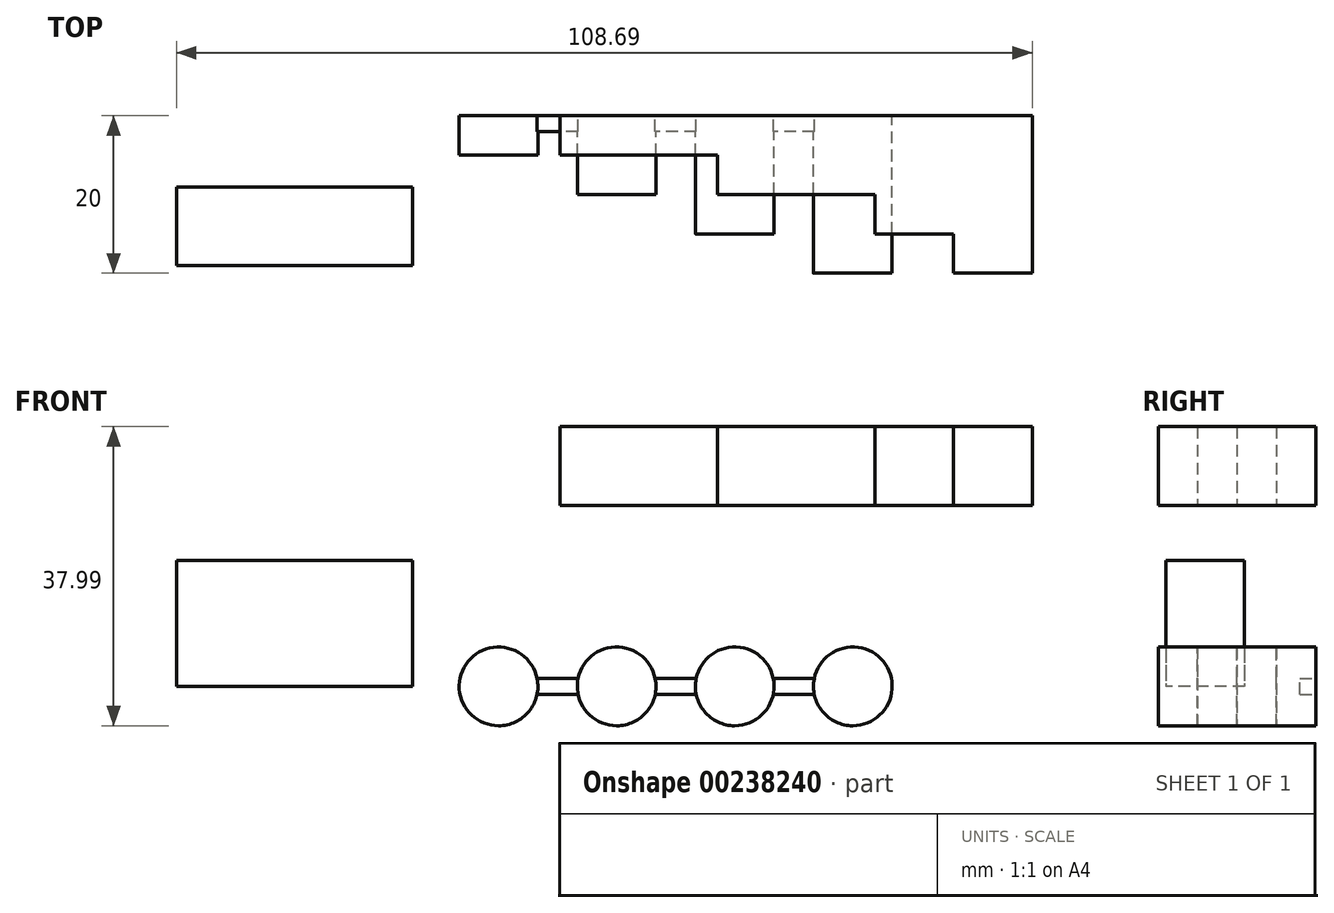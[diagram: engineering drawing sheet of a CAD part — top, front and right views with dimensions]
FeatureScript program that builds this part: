
annotation { "Feature Type Name" : "Feature", "Feature Type Description" : "" }
export const myFeature = defineFeature(function(context is Context, id is Id, definition is map)
    precondition{}
    {
        {
            var Q0;
            Q0=qCreatedBy(makeId("Front.planeOp"),FACE);
            var sketch = newSketch(context, id + "F0", { "sketchPlane" : qUnion([Q0])});
            skCircle(sketch, "E0", {"center": v(0, 0) * mm, "radius": 5 * mm});
            skCircle(sketch, "E1.1.0.0", {"center": v(15, 0) * mm, "radius": 5 * mm});
            skCircle(sketch, "E1.2.0.0", {"center": v(30, 0) * mm, "radius": 5 * mm});
            skCircle(sketch, "E1.3.0.0", {"center": v(45, 0) * mm, "radius": 5 * mm});
            skLineSegment(sketch, "E1.direction1", {"start": v(0, 0) * mm, "end": v(15, 0) * mm, "construction": true});
            skSolve(sketch);
        }
        {
            var Q0;
            Q0=makeQuery(id+"F0.imprint","IMPRINT",FACE,{"disambiguationData":[TD([[makeQuery(id+"F0.imprint","IMPRINT",EDGE,{"derivedFrom":sQuery(id+"F0.wireOp",EDGE,"E0")}),1.0]])]});
            extrude(context, id + "F1", {"entities" : qUnion([Q0]), "depth" : 5 * mm});
        }
        {
            var Q0;
            Q0=makeQuery(id+"F0.imprint","IMPRINT",FACE,{"disambiguationData":[TD([[makeQuery(id+"F0.imprint","IMPRINT",EDGE,{"derivedFrom":sQuery(id+"F0.wireOp",EDGE,"E1.1.0.0")}),1.0]])]});
            extrude(context, id + "F2", {"entities" : qUnion([Q0]), "depth" : 10 * mm});
        }
        {
            var Q0;
            Q0=makeQuery(id+"F0.imprint","IMPRINT",FACE,{"disambiguationData":[TD([[makeQuery(id+"F0.imprint","IMPRINT",EDGE,{"derivedFrom":sQuery(id+"F0.wireOp",EDGE,"E1.2.0.0")}),1.0]])]});
            extrude(context, id + "F3", {"entities" : qUnion([Q0]), "depth" : 15 * mm});
        }
        {
            var Q0;
            Q0=makeQuery(id+"F0.imprint","IMPRINT",FACE,{"disambiguationData":[TD([[makeQuery(id+"F0.imprint","IMPRINT",EDGE,{"derivedFrom":sQuery(id+"F0.wireOp",EDGE,"E1.3.0.0")}),1.0]])]});
            extrude(context, id + "F4", {"entities" : qUnion([Q0]), "depth" : 20 * mm});
        }
        {
            var Q0;
            Q0=makeQuery(id+"F0.imprint","IMPRINT",FACE,{"disambiguationData":[TD([[makeQuery(id+"F0.imprint","IMPRINT",EDGE,{"derivedFrom":sQuery(id+"F0.wireOp",EDGE,"E0")}),1.0]])]});
            var sketch = newSketch(context, id + "F5", { "sketchPlane" : qUnion([Q0])});
            skArc(sketch, "E2.0", {"start": v(45, -5) * mm, "mid": v(50, 0) * mm, "end": v(45, 5) * mm});
            skArc(sketch, "E2.1", {"start": v(0, 5) * mm, "mid": v(-5, 0) * mm, "end": v(0, -5) * mm});
            skLineSegment(sketch, "E3", {"start": v(45, -5) * mm, "end": v(0, -5) * mm});
            skLineSegment(sketch, "E4", {"start": v(0, 5) * mm, "end": v(45, 5) * mm});
            skSolve(sketch);
        }
        {
            var Q0;
            Q0=makeQuery(id+"F4.opExtrude","SWEPT_BODY",BODY,{"disambiguationData":[OSD([sQuery(id+"F0.wireOp",EDGE,"E1.3.0.0")])]});
            var Q1;
            Q1=makeQuery(id+"FrmGR7nz3px04QZ_4.opExtrude","SWEPT_BODY",BODY,{"disambiguationData":[OSD([sQuery(id+"F5.wireOp",EDGE,"E2.0"),sQuery(id+"F5.wireOp",EDGE,"E2.1"),sQuery(id+"F5.wireOp",EDGE,"E3"),sQuery(id+"F5.wireOp",EDGE,"E4")])]});
            var Q2;
            Q2=makeQuery(id+"F3.opExtrude","SWEPT_BODY",BODY,{"disambiguationData":[OSD([sQuery(id+"F0.wireOp",EDGE,"E1.2.0.0")])]});
            var Q3;
            Q3=makeQuery(id+"F2.opExtrude","SWEPT_BODY",BODY,{"disambiguationData":[OSD([sQuery(id+"F0.wireOp",EDGE,"E1.1.0.0")])]});
            var Q4;
            Q4=makeQuery(id+"F1.opExtrude","SWEPT_BODY",BODY,{"disambiguationData":[OSD([sQuery(id+"F0.wireOp",EDGE,"E0")])]});
            booleanBodies(context, id + "F6", {"operationType" : BooleanOperationType.UNION, "tools" : qUnion([Q0, Q1, Q2, Q3, Q4])});
        }
        {
            var Q0;
            Q0=makeQuery(id+"F6.opBoolean","MERGE",FACE,{"derivedFrom":[makeQuery(id+"F4.opExtrude","CAP_FACE",FACE,{"disambiguationData":[OSD([sQuery(id+"F0.wireOp",EDGE,"E1.3.0.0")])],"isStart":true}),makeQuery(id+"FrmGR7nz3px04QZ_4.opExtrude","CAP_FACE",FACE,{"disambiguationData":[OSD([sQuery(id+"F5.wireOp",EDGE,"E2.0"),sQuery(id+"F5.wireOp",EDGE,"E2.1"),sQuery(id+"F5.wireOp",EDGE,"E3"),sQuery(id+"F5.wireOp",EDGE,"E4")])],"isStart":true})]});
            var sketch = newSketch(context, id + "F7", { "sketchPlane" : qUnion([Q0])});
            skLineSegment(sketch, "E5.bottom", {"start": v(-67.8, 23) * mm, "end": v(-7.8, 23) * mm});
            skLineSegment(sketch, "E5.top", {"start": v(-67.8, 33) * mm, "end": v(-7.8, 33) * mm});
            skLineSegment(sketch, "E5.left", {"start": v(-67.8, 23) * mm, "end": v(-67.8, 33) * mm});
            skLineSegment(sketch, "E5.right", {"start": v(-7.8, 23) * mm, "end": v(-7.8, 33) * mm});
            skSolve(sketch);
        }
        {
            var Q0;
            Q0=makeQuery(id+"F7.imprint","IMPRINT",FACE,{"disambiguationData":[TD([[makeQuery(id+"F7.imprint","IMPRINT",EDGE,{"derivedFrom":sQuery(id+"F7.wireOp",EDGE,"E5.bottom")}),1.0]])]});
            extrude(context, id + "F8", {"entities" : qUnion([Q0]), "oppositeDirection" : true, "depth" : 5 * mm});
        }
        {
            var Q0;
            Q0=makeQuery(id+"F8.opExtrude","CAP_FACE",FACE,{"disambiguationData":[OSD([sQuery(id+"F7.wireOp",EDGE,"E5.bottom"),sQuery(id+"F7.wireOp",EDGE,"E5.top"),sQuery(id+"F7.wireOp",EDGE,"E5.left"),sQuery(id+"F7.wireOp",EDGE,"E5.right")])],"isStart":false});
            var sketch = newSketch(context, id + "F9", { "sketchPlane" : qUnion([Q0])});
            skLineSegment(sketch, "E6.bottom", {"start": v(67.8, 33) * mm, "end": v(27.8, 33) * mm});
            skLineSegment(sketch, "E6.top", {"start": v(67.8, 23) * mm, "end": v(27.8, 23) * mm});
            skLineSegment(sketch, "E6.left", {"start": v(67.8, 33) * mm, "end": v(67.8, 23) * mm});
            skLineSegment(sketch, "E6.right", {"start": v(27.8, 33) * mm, "end": v(27.8, 23) * mm});
            skSolve(sketch);
        }
        {
            var Q0;
            Q0=makeQuery(id+"F9.imprint","IMPRINT",FACE,{"disambiguationData":[TD([[makeQuery(id+"F9.imprint","IMPRINT",EDGE,{"derivedFrom":sQuery(id+"F9.wireOp",EDGE,"E6.bottom")}),1.0]])]});
            extrude(context, id + "F10", {"entities" : qUnion([Q0]), "operationType" : NewBodyOperationType.ADD, "depth" : 5 * mm});
        }
        {
            var Q0;
            Q0=makeQuery(id+"F10.opExtrude","CAP_FACE",FACE,{"disambiguationData":[OSD([sQuery(id+"F9.wireOp",EDGE,"E6.bottom"),sQuery(id+"F9.wireOp",EDGE,"E6.top"),sQuery(id+"F9.wireOp",EDGE,"E6.left"),sQuery(id+"F9.wireOp",EDGE,"E6.right")])],"isStart":false});
            var sketch = newSketch(context, id + "F11", { "sketchPlane" : qUnion([Q0])});
            skLineSegment(sketch, "E7.bottom", {"start": v(67.8, 33) * mm, "end": v(47.8, 33) * mm});
            skLineSegment(sketch, "E7.top", {"start": v(67.8, 23) * mm, "end": v(47.8, 23) * mm});
            skLineSegment(sketch, "E7.left", {"start": v(67.8, 33) * mm, "end": v(67.8, 23) * mm});
            skLineSegment(sketch, "E7.right", {"start": v(47.8, 33) * mm, "end": v(47.8, 23) * mm});
            skSolve(sketch);
        }
        {
            var Q0;
            Q0=makeQuery(id+"F11.imprint","IMPRINT",FACE,{"disambiguationData":[TD([[makeQuery(id+"F11.imprint","IMPRINT",EDGE,{"derivedFrom":sQuery(id+"F11.wireOp",EDGE,"E7.bottom")}),1.0]])]});
            extrude(context, id + "F12", {"entities" : qUnion([Q0]), "operationType" : NewBodyOperationType.ADD, "depth" : 5 * mm});
        }
        {
            var Q0;
            Q0=makeQuery(id+"F12.opExtrude","CAP_FACE",FACE,{"disambiguationData":[OSD([sQuery(id+"F11.wireOp",EDGE,"E7.bottom"),sQuery(id+"F11.wireOp",EDGE,"E7.top"),sQuery(id+"F11.wireOp",EDGE,"E7.left"),sQuery(id+"F11.wireOp",EDGE,"E7.right")])],"isStart":false});
            var sketch = newSketch(context, id + "F13", { "sketchPlane" : qUnion([Q0])});
            skLineSegment(sketch, "E8.bottom", {"start": v(67.8, 33) * mm, "end": v(57.8, 33) * mm});
            skLineSegment(sketch, "E8.top", {"start": v(67.8, 23) * mm, "end": v(57.8, 23) * mm});
            skLineSegment(sketch, "E8.left", {"start": v(67.8, 33) * mm, "end": v(67.8, 23) * mm});
            skLineSegment(sketch, "E8.right", {"start": v(57.8, 33) * mm, "end": v(57.8, 23) * mm});
            skSolve(sketch);
        }
        {
            var Q0;
            Q0=makeQuery(id+"F13.imprint","IMPRINT",FACE,{"disambiguationData":[TD([[makeQuery(id+"F13.imprint","IMPRINT",EDGE,{"derivedFrom":sQuery(id+"F13.wireOp",EDGE,"E8.bottom")}),1.0]])]});
            extrude(context, id + "F14", {"entities" : qUnion([Q0]), "operationType" : NewBodyOperationType.ADD, "depth" : 5 * mm});
        }
        {
            var Q0;
            {var subQ0=sQuery(id+"F5.wireOp",EDGE,"E2.1");Q0=makeQuery(id+"F5.imprint","IMPRINT",FACE,{"disambiguationData":[TD([[makeQuery(id+"F5.imprint","IMPRINT",EDGE,{"derivedFrom":subQ0}),1.0]])]});}
            var sketch = newSketch(context, id + "F15", { "sketchPlane" : qUnion([Q0])});
            skLineSegment(sketch, "E9.bottom", {"start": v(45.2, -1) * mm, "end": v(0.29, -1) * mm});
            skLineSegment(sketch, "E9.top", {"start": v(45.2, 1) * mm, "end": v(0.29, 1) * mm});
            skLineSegment(sketch, "E9.left", {"start": v(45.2, -1) * mm, "end": v(45.2, 1) * mm});
            skLineSegment(sketch, "E9.right", {"start": v(0.29, -1) * mm, "end": v(0.29, 1) * mm});
            skPoint(sketch, "E9.middle", {"position": v(22.75, 0) * mm});
            skSolve(sketch);
        }
        {
            var Q0;
            Q0=qSketchRegion(id+"F15",true);
            extrude(context, id + "F16", {"entities" : qUnion([Q0]), "operationType" : NewBodyOperationType.ADD, "depth" : 2 * mm});
        }
        {
            var Q0;
            Q0=qCreatedBy(makeId("Top.planeOp"),FACE);
            var sketch = newSketch(context, id + "F17", { "sketchPlane" : qUnion([Q0])});
            skLineSegment(sketch, "E10.bottom", {"start": v(-40.9, -9.03) * mm, "end": v(-10.9, -9.03) * mm});
            skLineSegment(sketch, "E10.top", {"start": v(-40.9, -19.03) * mm, "end": v(-10.9, -19.03) * mm});
            skLineSegment(sketch, "E10.left", {"start": v(-40.9, -9.03) * mm, "end": v(-40.9, -19.03) * mm});
            skLineSegment(sketch, "E10.right", {"start": v(-10.9, -9.03) * mm, "end": v(-10.9, -19.03) * mm});
            skSolve(sketch);
        }
        {
            var Q0;
            Q0=makeQuery(id+"F17.imprint","IMPRINT",FACE,{"disambiguationData":[TD([[makeQuery(id+"F17.imprint","IMPRINT",EDGE,{"derivedFrom":sQuery(id+"F17.wireOp",EDGE,"E10.bottom")}),-1.0]])]});
            extrude(context, id + "F18", {"entities" : qUnion([Q0]), "depth" : 16 * mm});
        }
    });
